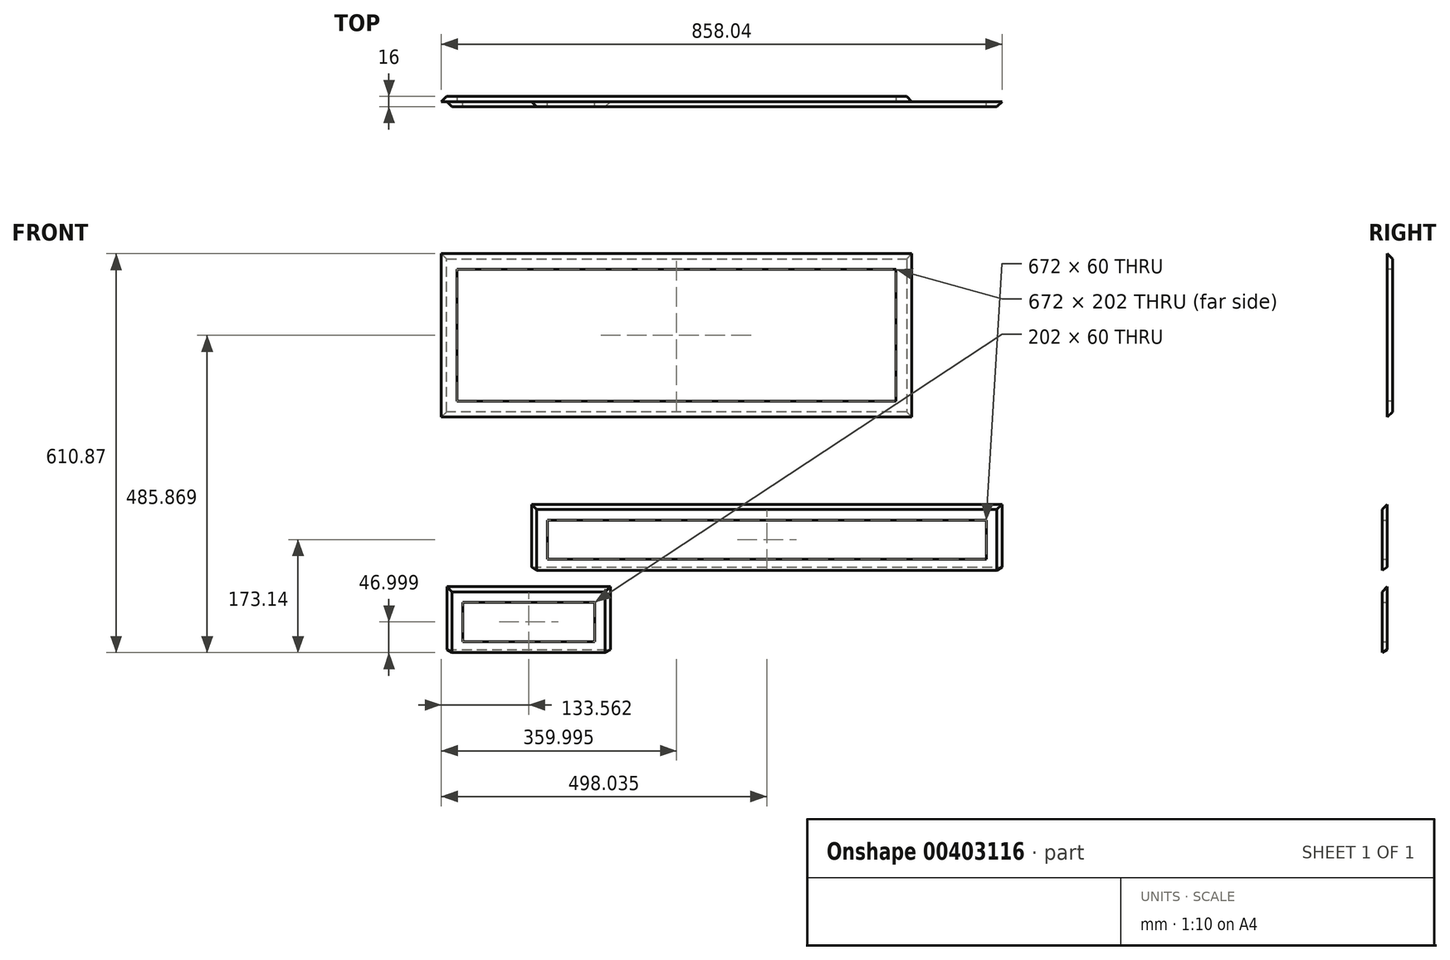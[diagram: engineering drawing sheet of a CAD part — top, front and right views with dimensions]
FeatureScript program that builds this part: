
annotation { "Feature Type Name" : "Feature", "Feature Type Description" : "" }
export const myFeature = defineFeature(function(context is Context, id is Id, definition is map)
    precondition{}
    {
        {
            var Q0;
            Q0=qCreatedBy(makeId("Front.planeOp"),FACE);
            var sketch = newSketch(context, id + "F0", { "sketchPlane" : qUnion([Q0])});
            skLineSegment(sketch, "E0.bottom", {"start": v(-165.5, 48.7) * mm, "end": v(554.5, 48.7) * mm});
            skLineSegment(sketch, "E0.top", {"start": v(-165.5, -47.3) * mm, "end": v(554.5, -47.3) * mm});
            skLineSegment(sketch, "E0.left", {"start": v(-165.5, 48.7) * mm, "end": v(-165.5, -47.3) * mm});
            skLineSegment(sketch, "E0.right", {"start": v(554.5, 48.7) * mm, "end": v(554.5, -47.3) * mm});
            skLineSegment(sketch, "E1.bottom", {"start": v(-165.5, 48.7) * mm, "end": v(-141.5, 48.7) * mm});
            skLineSegment(sketch, "E1.top", {"start": v(-165.5, 24.7) * mm, "end": v(-141.5, 24.7) * mm});
            skLineSegment(sketch, "E1.left", {"start": v(-165.5, 48.7) * mm, "end": v(-165.5, 24.7) * mm});
            skLineSegment(sketch, "E1.right", {"start": v(-141.5, 48.7) * mm, "end": v(-141.5, 24.7) * mm});
            skLineSegment(sketch, "E2.bottom", {"start": v(554.5, 48.7) * mm, "end": v(530.5, 48.7) * mm});
            skLineSegment(sketch, "E2.top", {"start": v(554.5, 24.7) * mm, "end": v(530.5, 24.7) * mm});
            skLineSegment(sketch, "E2.left", {"start": v(554.5, 48.7) * mm, "end": v(554.5, 24.7) * mm});
            skLineSegment(sketch, "E2.right", {"start": v(530.5, 48.7) * mm, "end": v(530.5, 24.7) * mm});
            skLineSegment(sketch, "E3", {"start": v(-141.5, 24.7) * mm, "end": v(530.5, 24.7) * mm});
            skLineSegment(sketch, "E4.bottom", {"start": v(-165.5, -47.3) * mm, "end": v(-141.5, -47.3) * mm});
            skLineSegment(sketch, "E4.top", {"start": v(-165.5, -35.3) * mm, "end": v(-141.5, -35.3) * mm});
            skLineSegment(sketch, "E4.left", {"start": v(-165.5, -47.3) * mm, "end": v(-165.5, -35.3) * mm});
            skLineSegment(sketch, "E4.right", {"start": v(-141.5, -47.3) * mm, "end": v(-141.5, -35.3) * mm});
            skLineSegment(sketch, "E5.bottom", {"start": v(554.5, -47.3) * mm, "end": v(530.5, -47.3) * mm});
            skLineSegment(sketch, "E5.top", {"start": v(554.5, -35.3) * mm, "end": v(530.5, -35.3) * mm});
            skLineSegment(sketch, "E5.left", {"start": v(554.5, -47.3) * mm, "end": v(554.5, -35.3) * mm});
            skLineSegment(sketch, "E5.right", {"start": v(530.5, -47.3) * mm, "end": v(530.5, -35.3) * mm});
            skLineSegment(sketch, "E6", {"start": v(-141.5, -35.3) * mm, "end": v(530.5, -35.3) * mm});
            skLineSegment(sketch, "E7", {"start": v(-141.5, 24.7) * mm, "end": v(-141.5, -35.3) * mm});
            skLineSegment(sketch, "E8", {"start": v(530.5, 24.7) * mm, "end": v(530.5, -35.3) * mm});
            skSolve(sketch);
        }
        {
            var Q0;
            Q0=makeQuery(id+"F0.imprint","IMPRINT",FACE,{"disambiguationData":[TD([[makeQuery(id+"F0.imprint","IMPRINT",EDGE,{"derivedFrom":sQuery(id+"F0.wireOp",EDGE,"E0.bottom")}),-1.0]])]});
            var Q1;
            Q1=makeQuery(id+"F0.imprint","IMPRINT",FACE,{"disambiguationData":[TD([[makeQuery(id+"F0.imprint","IMPRINT",EDGE,{"derivedFrom":sQuery(id+"F0.wireOp",EDGE,"E1.bottom")}),-1.0]])]});
            var Q2;
            Q2=makeQuery(id+"F0.imprint","IMPRINT",FACE,{"disambiguationData":[TD([[makeQuery(id+"F0.imprint","IMPRINT",EDGE,{"derivedFrom":sQuery(id+"F0.wireOp",EDGE,"E0.left")}),1.0]])]});
            var Q3;
            Q3=makeQuery(id+"F0.imprint","IMPRINT",FACE,{"disambiguationData":[TD([[makeQuery(id+"F0.imprint","IMPRINT",EDGE,{"derivedFrom":sQuery(id+"F0.wireOp",EDGE,"E4.bottom")}),1.0]])]});
            var Q4;
            Q4=makeQuery(id+"F0.imprint","IMPRINT",FACE,{"disambiguationData":[TD([[makeQuery(id+"F0.imprint","IMPRINT",EDGE,{"derivedFrom":sQuery(id+"F0.wireOp",EDGE,"E0.top")}),1.0]])]});
            var Q5;
            Q5=makeQuery(id+"F0.imprint","IMPRINT",FACE,{"disambiguationData":[TD([[makeQuery(id+"F0.imprint","IMPRINT",EDGE,{"derivedFrom":sQuery(id+"F0.wireOp",EDGE,"E0.right")}),-1.0]])]});
            var Q6;
            Q6=makeQuery(id+"F0.imprint","IMPRINT",FACE,{"disambiguationData":[TD([[makeQuery(id+"F0.imprint","IMPRINT",EDGE,{"derivedFrom":sQuery(id+"F0.wireOp",EDGE,"E2.bottom")}),1.0]])]});
            var Q7;
            Q7=makeQuery(id+"F0.imprint","IMPRINT",FACE,{"disambiguationData":[TD([[makeQuery(id+"F0.imprint","IMPRINT",EDGE,{"derivedFrom":sQuery(id+"F0.wireOp",EDGE,"E5.bottom")}),-1.0]])]});
            extrude(context, id + "F1", {"entities" : qUnion([Q0, Q1, Q2, Q3, Q4, Q5, Q6, Q7]), "depth" : 8 * mm});
        }
        {
            var Q0;
            Q0=makeQuery(id+"F1.opExtrude","SWEPT_FACE",FACE,{"disambiguationData":[OSD([sQuery(id+"F0.wireOp",EDGE,"E0.left"),sQuery(id+"F0.wireOp",EDGE,"E1.left"),sQuery(id+"F0.wireOp",EDGE,"E4.left")])]});
            var sketch = newSketch(context, id + "F2", { "sketchPlane" : qUnion([Q0])});
            skLineSegment(sketch, "E9", {"start": v(8, -47.3) * mm, "end": v(8, -52.3) * mm});
            skLineSegment(sketch, "E10", {"start": v(0, -47.3) * mm, "end": v(8, -52.3) * mm});
            skSolve(sketch);
        }
        {
            var Q0;
            Q0 = qSketchRegion(id + "F2", true);
            var Q1;
            Q1=makeQuery(id+"F2.imprint","IMPRINT",FACE,{"disambiguationData":[TD([[makeQuery(id+"F2.imprint","IMPRINT",EDGE,{"derivedFrom":sQuery(id+"F2.wireOp",EDGE,"E9")}),-1.0]])]});
            extrude(context, id + "F3", {"entities" : qUnion([Q0, Q1]), "operationType" : NewBodyOperationType.ADD, "oppositeDirection" : true, "depth" : 720 * mm});
        }
        {
            var Q0;
            Q0=makeQuery(id+"F3.boolean.opBoolean","MERGE",EDGE,{"derivedFrom":[makeQuery(id+"F1.opExtrude","CAP_EDGE",EDGE,{"disambiguationData":[OSD([sQuery(id+"F0.wireOp",EDGE,"E0.right"),sQuery(id+"F0.wireOp",EDGE,"E2.left"),sQuery(id+"F0.wireOp",EDGE,"E5.left")])],"isStart":false}),makeQuery(id+"F3.opExtrude","CAP_EDGE",EDGE,{"disambiguationData":[OSD([sQuery(id+"F2.wireOp",EDGE,"E9")])],"isStart":false})]});
            var Q1;
            Q1=makeQuery(id+"F1.opExtrude","CAP_EDGE",EDGE,{"disambiguationData":[OSD([sQuery(id+"F0.wireOp",EDGE,"E0.bottom"),sQuery(id+"F0.wireOp",EDGE,"E1.bottom"),sQuery(id+"F0.wireOp",EDGE,"E2.bottom")])],"isStart":false});
            var Q2;
            Q2=makeQuery(id+"F3.boolean.opBoolean","MERGE",EDGE,{"derivedFrom":[makeQuery(id+"F1.opExtrude","CAP_EDGE",EDGE,{"disambiguationData":[OSD([sQuery(id+"F0.wireOp",EDGE,"E0.left"),sQuery(id+"F0.wireOp",EDGE,"E1.left"),sQuery(id+"F0.wireOp",EDGE,"E4.left")])],"isStart":false}),makeQuery(id+"F3.opExtrude","CAP_EDGE",EDGE,{"disambiguationData":[OSD([sQuery(id+"F2.wireOp",EDGE,"E9")])],"isStart":true})]});
            chamfer(context, id + "F4", {"entities" : qUnion([Q0, Q1, Q2]), "width" : 8 * mm, "tangentPropagation" : true});
        }
        {
            var Q0;
            Q0=qCreatedBy(makeId("Front.planeOp"),FACE);
            var sketch = newSketch(context, id + "F5", { "sketchPlane" : qUnion([Q0])});
            skLineSegment(sketch, "E11.bottom", {"start": v(-294.97, -77.45) * mm, "end": v(-44.97, -77.45) * mm});
            skLineSegment(sketch, "E11.top", {"start": v(-294.97, -173.45) * mm, "end": v(-44.97, -173.45) * mm});
            skLineSegment(sketch, "E11.left", {"start": v(-294.97, -77.45) * mm, "end": v(-294.97, -173.45) * mm});
            skLineSegment(sketch, "E11.right", {"start": v(-44.97, -77.45) * mm, "end": v(-44.97, -173.45) * mm});
            skLineSegment(sketch, "E12.bottom", {"start": v(-294.97, -77.45) * mm, "end": v(-270.97, -77.45) * mm});
            skLineSegment(sketch, "E12.top", {"start": v(-294.97, -101.45) * mm, "end": v(-270.97, -101.45) * mm});
            skLineSegment(sketch, "E12.left", {"start": v(-294.97, -77.45) * mm, "end": v(-294.97, -101.45) * mm});
            skLineSegment(sketch, "E12.right", {"start": v(-270.97, -77.45) * mm, "end": v(-270.97, -101.45) * mm});
            skLineSegment(sketch, "E13.bottom", {"start": v(-44.97, -77.45) * mm, "end": v(-68.97, -77.45) * mm});
            skLineSegment(sketch, "E13.top", {"start": v(-44.97, -101.45) * mm, "end": v(-68.97, -101.45) * mm});
            skLineSegment(sketch, "E13.left", {"start": v(-44.97, -77.45) * mm, "end": v(-44.97, -101.45) * mm});
            skLineSegment(sketch, "E13.right", {"start": v(-68.97, -77.45) * mm, "end": v(-68.97, -101.45) * mm});
            skLineSegment(sketch, "E14.bottom", {"start": v(-294.97, -173.45) * mm, "end": v(-270.97, -173.45) * mm});
            skLineSegment(sketch, "E14.top", {"start": v(-294.97, -161.45) * mm, "end": v(-270.97, -161.45) * mm});
            skLineSegment(sketch, "E14.left", {"start": v(-294.97, -173.45) * mm, "end": v(-294.97, -161.45) * mm});
            skLineSegment(sketch, "E14.right", {"start": v(-270.97, -173.45) * mm, "end": v(-270.97, -161.45) * mm});
            skLineSegment(sketch, "E15.bottom", {"start": v(-44.97, -173.45) * mm, "end": v(-68.97, -173.45) * mm});
            skLineSegment(sketch, "E15.top", {"start": v(-44.97, -161.45) * mm, "end": v(-68.97, -161.45) * mm});
            skLineSegment(sketch, "E15.left", {"start": v(-44.97, -173.45) * mm, "end": v(-44.97, -161.45) * mm});
            skLineSegment(sketch, "E15.right", {"start": v(-68.97, -173.45) * mm, "end": v(-68.97, -161.45) * mm});
            skLineSegment(sketch, "E16", {"start": v(-270.97, -101.45) * mm, "end": v(-68.97, -101.45) * mm});
            skLineSegment(sketch, "E17", {"start": v(-270.97, -101.45) * mm, "end": v(-270.97, -161.45) * mm});
            skLineSegment(sketch, "E18", {"start": v(-68.97, -101.45) * mm, "end": v(-68.97, -161.45) * mm});
            skLineSegment(sketch, "E19", {"start": v(-68.97, -161.45) * mm, "end": v(-270.97, -161.45) * mm});
            skSolve(sketch);
        }
        {
            var Q0;
            Q0=makeQuery(id+"F5.imprint","IMPRINT",FACE,{"disambiguationData":[TD([[makeQuery(id+"F5.imprint","IMPRINT",EDGE,{"derivedFrom":sQuery(id+"F5.wireOp",EDGE,"E11.bottom")}),-1.0]])]});
            var Q1;
            Q1=makeQuery(id+"F5.imprint","IMPRINT",FACE,{"disambiguationData":[TD([[makeQuery(id+"F5.imprint","IMPRINT",EDGE,{"derivedFrom":sQuery(id+"F5.wireOp",EDGE,"E12.bottom")}),-1.0]])]});
            var Q2;
            Q2=makeQuery(id+"F5.imprint","IMPRINT",FACE,{"disambiguationData":[TD([[makeQuery(id+"F5.imprint","IMPRINT",EDGE,{"derivedFrom":sQuery(id+"F5.wireOp",EDGE,"E11.left")}),1.0]])]});
            var Q3;
            Q3=makeQuery(id+"F5.imprint","IMPRINT",FACE,{"disambiguationData":[TD([[makeQuery(id+"F5.imprint","IMPRINT",EDGE,{"derivedFrom":sQuery(id+"F5.wireOp",EDGE,"E14.bottom")}),1.0]])]});
            var Q4;
            Q4=makeQuery(id+"F5.imprint","IMPRINT",FACE,{"disambiguationData":[TD([[makeQuery(id+"F5.imprint","IMPRINT",EDGE,{"derivedFrom":sQuery(id+"F5.wireOp",EDGE,"E11.top")}),1.0]])]});
            var Q5;
            Q5=makeQuery(id+"F5.imprint","IMPRINT",FACE,{"disambiguationData":[TD([[makeQuery(id+"F5.imprint","IMPRINT",EDGE,{"derivedFrom":sQuery(id+"F5.wireOp",EDGE,"E15.bottom")}),-1.0]])]});
            var Q6;
            Q6=makeQuery(id+"F5.imprint","IMPRINT",FACE,{"disambiguationData":[TD([[makeQuery(id+"F5.imprint","IMPRINT",EDGE,{"derivedFrom":sQuery(id+"F5.wireOp",EDGE,"E11.right")}),-1.0]])]});
            var Q7;
            Q7=makeQuery(id+"F5.imprint","IMPRINT",FACE,{"disambiguationData":[TD([[makeQuery(id+"F5.imprint","IMPRINT",EDGE,{"derivedFrom":sQuery(id+"F5.wireOp",EDGE,"E13.bottom")}),1.0]])]});
            extrude(context, id + "F6", {"entities" : qUnion([Q0, Q1, Q2, Q3, Q4, Q5, Q6, Q7]), "depth" : 8 * mm});
        }
        {
            var Q0;
            Q0=makeQuery(id+"F6.opExtrude","SWEPT_FACE",FACE,{"disambiguationData":[OSD([sQuery(id+"F5.wireOp",EDGE,"E11.left"),sQuery(id+"F5.wireOp",EDGE,"E12.left"),sQuery(id+"F5.wireOp",EDGE,"E14.left")])]});
            var sketch = newSketch(context, id + "F7", { "sketchPlane" : qUnion([Q0])});
            skLineSegment(sketch, "E20", {"start": v(8, -173.45) * mm, "end": v(8, -178.45) * mm});
            skLineSegment(sketch, "E21", {"start": v(0, -173.45) * mm, "end": v(8, -178.45) * mm});
            skSolve(sketch);
        }
        {
            var Q0;
            Q0 = qSketchRegion(id + "F7", true);
            var Q1;
            Q1=makeQuery(id+"F7.imprint","IMPRINT",FACE,{"disambiguationData":[TD([[makeQuery(id+"F7.imprint","IMPRINT",EDGE,{"derivedFrom":sQuery(id+"F7.wireOp",EDGE,"E20")}),-1.0]])]});
            extrude(context, id + "F8", {"entities" : qUnion([Q0, Q1]), "operationType" : NewBodyOperationType.ADD, "oppositeDirection" : true, "depth" : 250 * mm});
        }
        {
            var Q0;
            Q0=makeQuery(id+"F6.opExtrude","CAP_EDGE",EDGE,{"disambiguationData":[OSD([sQuery(id+"F5.wireOp",EDGE,"E11.bottom"),sQuery(id+"F5.wireOp",EDGE,"E12.bottom"),sQuery(id+"F5.wireOp",EDGE,"E13.bottom")])],"isStart":false});
            var Q1;
            Q1=makeQuery(id+"F8.boolean.opBoolean","MERGE",EDGE,{"derivedFrom":[makeQuery(id+"F6.opExtrude","CAP_EDGE",EDGE,{"disambiguationData":[OSD([sQuery(id+"F5.wireOp",EDGE,"E11.left"),sQuery(id+"F5.wireOp",EDGE,"E12.left"),sQuery(id+"F5.wireOp",EDGE,"E14.left")])],"isStart":false}),makeQuery(id+"F8.opExtrude","CAP_EDGE",EDGE,{"disambiguationData":[OSD([sQuery(id+"F7.wireOp",EDGE,"E20")])],"isStart":true})]});
            var Q2;
            Q2=makeQuery(id+"F8.boolean.opBoolean","MERGE",EDGE,{"derivedFrom":[makeQuery(id+"F6.opExtrude","CAP_EDGE",EDGE,{"disambiguationData":[OSD([sQuery(id+"F5.wireOp",EDGE,"E11.right"),sQuery(id+"F5.wireOp",EDGE,"E13.left"),sQuery(id+"F5.wireOp",EDGE,"E15.left")])],"isStart":false}),makeQuery(id+"F8.opExtrude","CAP_EDGE",EDGE,{"disambiguationData":[OSD([sQuery(id+"F7.wireOp",EDGE,"E20")])],"isStart":false})]});
            chamfer(context, id + "F9", {"entities" : qUnion([Q0, Q1, Q2]), "width" : 8 * mm, "tangentPropagation" : true});
        }
        {
            var Q0;
            Q0=qCreatedBy(makeId("Front.planeOp"),FACE);
            var sketch = newSketch(context, id + "F10", { "sketchPlane" : qUnion([Q0])});
            skLineSegment(sketch, "E22.bottom", {"start": v(416.47, 182.42) * mm, "end": v(-303.53, 182.42) * mm});
            skLineSegment(sketch, "E22.top", {"start": v(416.47, 432.42) * mm, "end": v(-303.53, 432.42) * mm});
            skLineSegment(sketch, "E22.left", {"start": v(416.47, 182.42) * mm, "end": v(416.47, 432.42) * mm});
            skLineSegment(sketch, "E22.right", {"start": v(-303.53, 182.42) * mm, "end": v(-303.53, 432.42) * mm});
            skSolve(sketch);
        }
        {
            var Q0;
            Q0 = qSketchRegion(id + "F10", true);
            extrude(context, id + "F11", {"entities" : qUnion([Q0]), "oppositeDirection" : true, "depth" : 8 * mm});
        }
        {
            var Q0;
            Q0=makeQuery(id+"F11.opExtrude","CAP_FACE",FACE,{"disambiguationData":[OSD([sQuery(id+"F10.wireOp",EDGE,"E22.bottom"),sQuery(id+"F10.wireOp",EDGE,"E22.top"),sQuery(id+"F10.wireOp",EDGE,"E22.left"),sQuery(id+"F10.wireOp",EDGE,"E22.right")])],"isStart":false});
            chamfer(context, id + "F12", {"entities" : qUnion([Q0]), "width" : 8 * mm, "tangentPropagation" : true});
        }
        {
            var Q0;
            Q0=makeQuery(id+"F11.opExtrude","CAP_FACE",FACE,{"disambiguationData":[OSD([sQuery(id+"F10.wireOp",EDGE,"E22.bottom"),sQuery(id+"F10.wireOp",EDGE,"E22.top"),sQuery(id+"F10.wireOp",EDGE,"E22.left"),sQuery(id+"F10.wireOp",EDGE,"E22.right")])],"isStart":true});
            var sketch = newSketch(context, id + "F13", { "sketchPlane" : qUnion([Q0])});
            skLineSegment(sketch, "E23.bottom", {"start": v(416.47, 182.42) * mm, "end": v(392.47, 182.42) * mm});
            skLineSegment(sketch, "E23.top", {"start": v(416.47, 206.42) * mm, "end": v(392.47, 206.42) * mm});
            skLineSegment(sketch, "E23.left", {"start": v(416.47, 182.42) * mm, "end": v(416.47, 206.42) * mm});
            skLineSegment(sketch, "E23.right", {"start": v(392.47, 182.42) * mm, "end": v(392.47, 206.42) * mm});
            skLineSegment(sketch, "E24.bottom", {"start": v(-303.53, 182.42) * mm, "end": v(-279.53, 182.42) * mm});
            skLineSegment(sketch, "E24.top", {"start": v(-303.53, 206.42) * mm, "end": v(-279.53, 206.42) * mm});
            skLineSegment(sketch, "E24.left", {"start": v(-303.53, 182.42) * mm, "end": v(-303.53, 206.42) * mm});
            skLineSegment(sketch, "E24.right", {"start": v(-279.53, 182.42) * mm, "end": v(-279.53, 206.42) * mm});
            skLineSegment(sketch, "E25.bottom", {"start": v(416.47, 432.42) * mm, "end": v(392.47, 432.42) * mm});
            skLineSegment(sketch, "E25.top", {"start": v(416.47, 408.42) * mm, "end": v(392.47, 408.42) * mm});
            skLineSegment(sketch, "E25.left", {"start": v(416.47, 432.42) * mm, "end": v(416.47, 408.42) * mm});
            skLineSegment(sketch, "E25.right", {"start": v(392.47, 432.42) * mm, "end": v(392.47, 408.42) * mm});
            skLineSegment(sketch, "E26.bottom", {"start": v(-303.53, 432.42) * mm, "end": v(-279.53, 432.42) * mm});
            skLineSegment(sketch, "E26.top", {"start": v(-303.53, 408.42) * mm, "end": v(-279.53, 408.42) * mm});
            skLineSegment(sketch, "E26.left", {"start": v(-303.53, 432.42) * mm, "end": v(-303.53, 408.42) * mm});
            skLineSegment(sketch, "E26.right", {"start": v(-279.53, 432.42) * mm, "end": v(-279.53, 408.42) * mm});
            skLineSegment(sketch, "E27", {"start": v(392.47, 206.42) * mm, "end": v(-279.53, 206.42) * mm});
            skLineSegment(sketch, "E28", {"start": v(-279.53, 408.42) * mm, "end": v(-279.53, 206.42) * mm});
            skLineSegment(sketch, "E29", {"start": v(-279.53, 408.42) * mm, "end": v(392.47, 408.42) * mm});
            skLineSegment(sketch, "E30", {"start": v(392.47, 408.42) * mm, "end": v(392.47, 206.42) * mm});
            skSolve(sketch);
        }
        {
            var Q0;
            Q0=makeQuery(id+"F13.imprint","IMPRINT",FACE,{"disambiguationData":[TD([[makeQuery(id+"F13.imprint","IMPRINT",EDGE,{"derivedFrom":sQuery(id+"F13.wireOp",EDGE,"E27")}),-1.0]])]});
            extrude(context, id + "F14", {"entities" : qUnion([Q0]), "operationType" : NewBodyOperationType.REMOVE, "oppositeDirection" : true, "depth" : 25 * mm});
        }
    });
